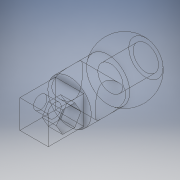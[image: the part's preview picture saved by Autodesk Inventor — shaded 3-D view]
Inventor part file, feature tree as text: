
AUTODESK INVENTOR PART (.ipt)
format: ipt  version: 2017 (Build 210142000, 142)  size: 253,952 bytes
history: native  units: mm
features: sketch x5, extrude x4, revolve x1, projected_geometry x1
ambient origin geometry x8: Origin, YZ Plane, XZ Plane, XY Plane, X Axis, Y Axis, Z Axis, Center Point
bodies: Solid1 (feature_tree)
feature tree (11):
  revolve  "Revolution1"  Angle=90.0deg
  extrude  "Extrusion1"  Depth=2.0mm
  extrude  "Extrusion2"  Depth=10.0mm TaperAngle=0.0deg
  extrude  "Extrusion5"  Depth=10.0mm TaperAngle=0.0deg
  extrude  "Extrusion6"  Depth=1.0mm
  sketch  "Sketch1"  dims[d2=3.8mm d3=2.0mm d4=2.0mm d5=16.0mm d6=2.0mm d7=16.0mm d8=90.0deg]
  sketch  "Sketch2"  dims[d9=3.8mm d10=2.0mm]
  projected_geometry  "Projected Loop1"
  sketch  "Sketch4"  dims[d17=5.0mm d18=10.0mm d19=0.0mm]
  sketch  "Sketch7"  dims[d24=10.0mm d25=0.0mm d27=5.0mm d28=0.0mm]
  sketch  "Sketch8"  dims[d37=3.0mm d42=3.8mm d43=2.0mm d44=3.5mm d45=7.35mm d46=3.0mm d47=1.0mm d48=180.0deg d49=2.0mm d50=6.0mm d51=3.0mm d52=1.0mm d53=180.0deg d54=2.0mm d62=10.0mm d63=0.0mm d64=7.79368mm d65=15.388mm d66=7.12mm d67=10.0mm d68=0.0mm d70=4.0mm d71=4.0mm d72=8.0mm d73=8.0mm]
